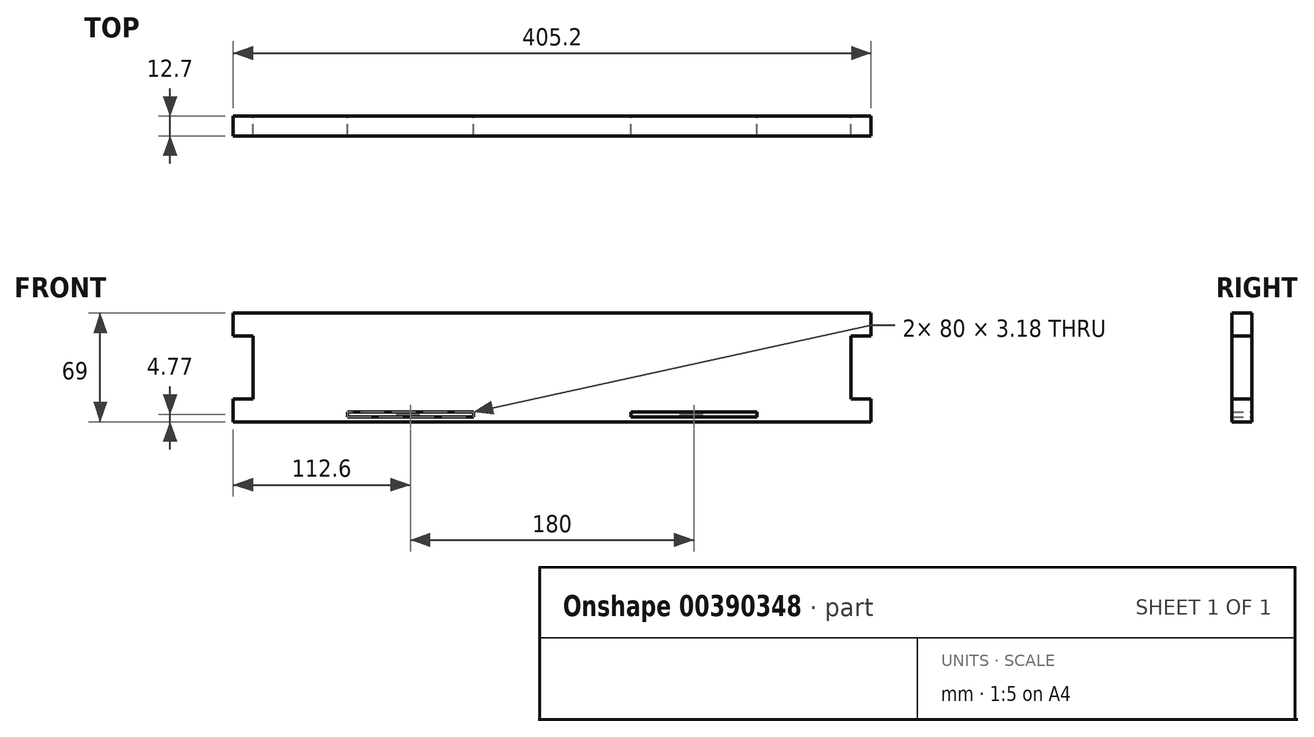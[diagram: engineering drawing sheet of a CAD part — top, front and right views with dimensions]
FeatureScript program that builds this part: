
annotation { "Feature Type Name" : "Feature", "Feature Type Description" : "" }
export const myFeature = defineFeature(function(context is Context, id is Id, definition is map)
    precondition{}
    {
        {
            assignVariable(context, id + "F0", {"name" : "MW", "anyValue" : 12.7});
        }
        {
            var Q0;
            Q0=qCreatedBy(makeId("Front.planeOp"),FACE);
            var sketch = newSketch(context, id + "F1", { "sketchPlane" : qUnion([Q0])});
            skLineSegment(sketch, "E0.bottom", {"start": v(202.6, -3.18) * mm, "end": v(-202.6, -3.18) * mm});
            skLineSegment(sketch, "E0.top", {"start": v(202.6, 65.82) * mm, "end": v(-202.6, 65.82) * mm});
            skLineSegment(sketch, "E0.left", {"start": v(202.6, -3.18) * mm, "end": v(202.6, 11.32) * mm});
            skLineSegment(sketch, "E0.right", {"start": v(-202.6, -3.18) * mm, "end": v(-202.6, 11.32) * mm});
            skPoint(sketch, "E0.middle", {"position": v(0, 31.32) * mm});
            skLineSegment(sketch, "E1", {"start": v(-202.6, 31.32) * mm, "end": v(0, 31.32) * mm, "construction": true});
            skLineSegment(sketch, "E2.bottom", {"start": v(-50, 0) * mm, "end": v(-130, 0) * mm});
            skLineSegment(sketch, "E2.top", {"start": v(-50, 3.18) * mm, "end": v(-130, 3.18) * mm});
            skLineSegment(sketch, "E2.left", {"start": v(-50, 0) * mm, "end": v(-50, 3.18) * mm});
            skLineSegment(sketch, "E2.right", {"start": v(-130, 0) * mm, "end": v(-130, 3.18) * mm});
            skPoint(sketch, "E2.middle", {"position": v(-90, 1.6) * mm});
            skLineSegment(sketch, "E3.bottom", {"start": v(-202.6, 11.32) * mm, "end": v(-189.9, 11.32) * mm});
            skLineSegment(sketch, "E3.top", {"start": v(-202.6, 51.32) * mm, "end": v(-189.9, 51.32) * mm});
            skLineSegment(sketch, "E3.right", {"start": v(-189.9, 11.32) * mm, "end": v(-189.9, 51.32) * mm});
            skPoint(sketch, "E3.middle", {"position": v(-196.25, 31.32) * mm});
            skLineSegment(sketch, "E4.trimOffspring", {"start": v(-202.6, 51.32) * mm, "end": v(-202.6, 65.82) * mm});
            skLineSegment(sketch, "E5.MirrorCS", {"start": v(130, 0) * mm, "end": v(130, 3.18) * mm});
            skLineSegment(sketch, "E6.MirrorCS", {"start": v(50, 0) * mm, "end": v(50, 3.18) * mm});
            skLineSegment(sketch, "E7.MirrorCS", {"start": v(50, 3.18) * mm, "end": v(130, 3.18) * mm});
            skLineSegment(sketch, "E8.MirrorCS", {"start": v(50, 0) * mm, "end": v(130, 0) * mm});
            skPoint(sketch, "E9.MirrorP", {"position": v(90, 1.6) * mm});
            skLineSegment(sketch, "E10.MirrorCS", {"start": v(189.9, 11.32) * mm, "end": v(189.9, 51.32) * mm});
            skLineSegment(sketch, "E11.MirrorCS", {"start": v(202.6, 11.32) * mm, "end": v(189.9, 11.32) * mm});
            skLineSegment(sketch, "E12.MirrorCS", {"start": v(202.6, 51.32) * mm, "end": v(189.9, 51.32) * mm});
            skPoint(sketch, "E13.MirrorP", {"position": v(196.25, 31.32) * mm});
            skLineSegment(sketch, "E14.trimOffspring", {"start": v(202.6, 51.32) * mm, "end": v(202.6, 65.82) * mm});
            skSolve(sketch);
        }
        {
            var Q0;
            Q0 = qSketchRegion(id + "F1", true);
            extrude(context, id + "F2", {"entities" : qUnion([Q0]), "depth" : (getVariable(context, 'MW')) * mm});
        }
    });
